# Revit family: AIRO
name_source: partatom
category: Lighting Fixtures
revit_build: Autodesk Revit 2013 (Build: 20120221_2030(x64)
units: mm (PartAtom-declared; Revit-internal decimal feet)

## types (5) — shared parameters
Apparent Load = 123 VA
Color Filter = 16777215
Default Elevation = 48 "
Description = Airo Roadway Luminaire
Dimming Lamp Color Temperature Shift = <None>
Emit Shape Visible in Rendering = No
Glass = Hubbell-White Glass
Lamp = LED Lamp
Load Classification = Lighting
Manufacturer = Hubbell Outdoor Lighting
Manufacturer Fax = 866-898-1065
Model = AIRO
Photometric Link = http://www.hubbelloutdoor.com
Photometric Web File = ASL-16L-3K-210-2.IES
Pole Height = 120 "
Power Factor = 1
Product Documentation Link = http://cdn.hubbelloutdoor.com
Product Page URL = http://www.hubbelloutdoor.com
Row Length = 22.4 "
Tilt Angle = 90.00°
URL = http://www.hubbelloutdoor.com
Voltage = 120 V
Wattage Comments = 62-225 W
Watts = 123 W

## per-type parameters (varying)
| type | Backbox | Emit from Rectangle Length | Emit from Rectangle Width | Types |
| ASL-Gray | Hubbell- Gray | 48 " | 24 " | AIRO Retrofit : ASL-16L |
| ASL-Black | Hubbell-Black | 48 " | 24 " | AIRO Retrofit : ASL-16L |
| ASL-Dark Bronze | Hubbell-Dark Bronze | 6 " | 8 " | AIRO Retrofit : ASL-8L |
| ASL-White | Hubbell-White | 48 " | 24 " | AIRO Retrofit : ASL-16L |
| ASL-Platinum Smooth | Hubbell- Platinum Smooth | 48 " | 24 " | AIRO Retrofit : ASL-16L |

## geometry (parser evidence)
native form markers: Blend x17, Sweep x2
no freeform markers — native parametric forms only
